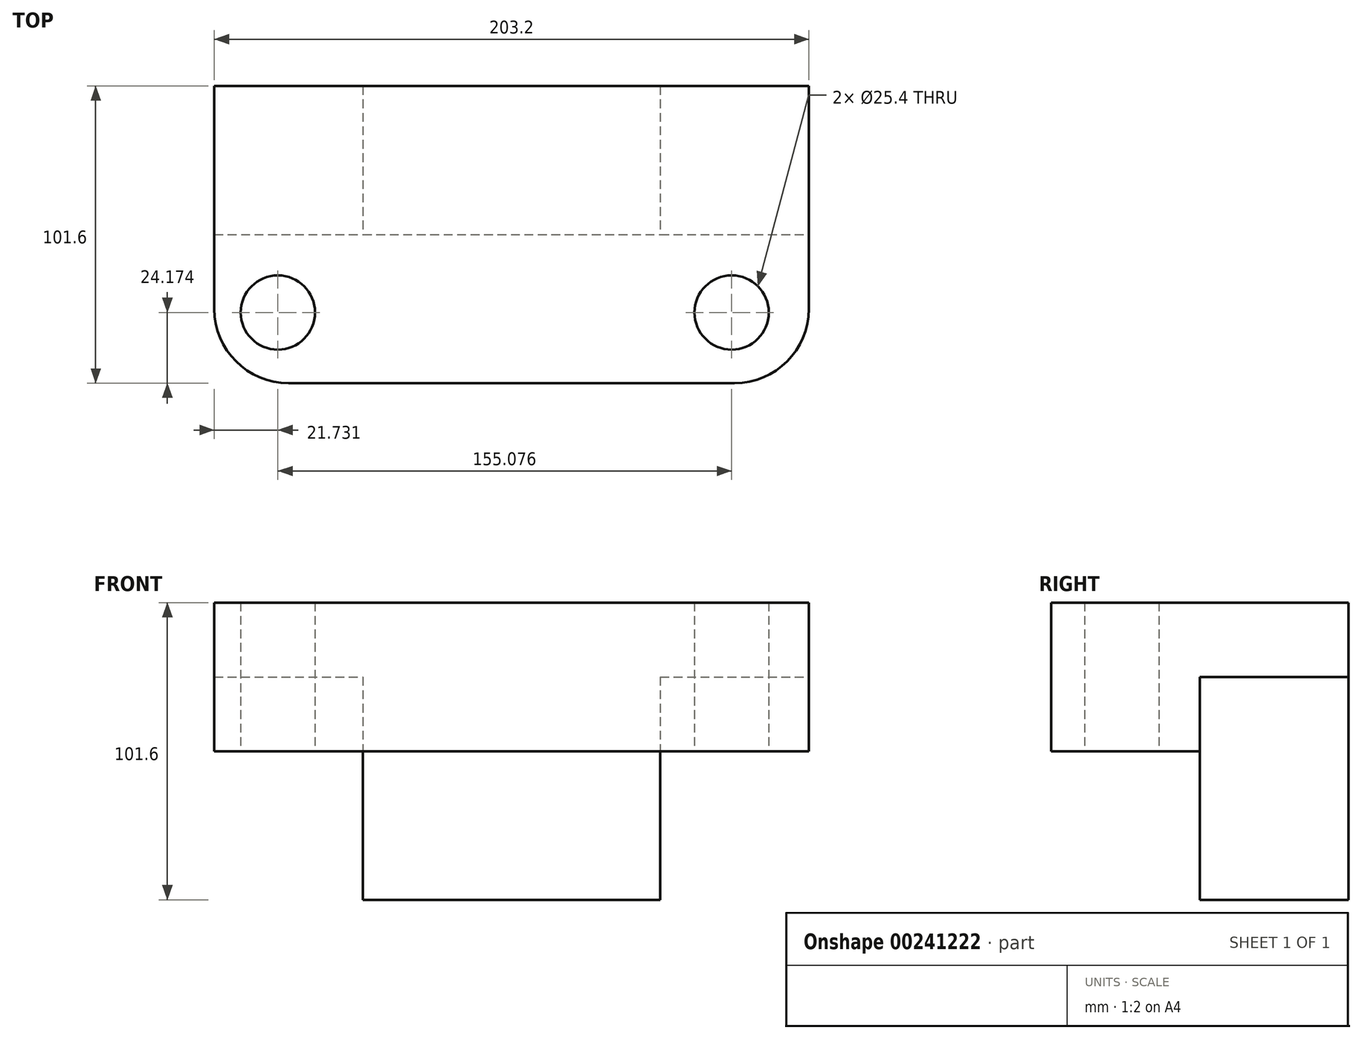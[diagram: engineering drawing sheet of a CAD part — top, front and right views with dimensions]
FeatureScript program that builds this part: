
annotation { "Feature Type Name" : "Feature", "Feature Type Description" : "" }
export const myFeature = defineFeature(function(context is Context, id is Id, definition is map)
    precondition{}
    {
        {
            var Q0;
            Q0=qCreatedBy(makeId("Front.planeOp"),FACE);
            var sketch = newSketch(context, id + "F0", { "sketchPlane" : qUnion([Q0])});
            skLineSegment(sketch, "E0.bottom", {"start": v(-115.86, 69.09) * mm, "end": v(87.34, 69.09) * mm});
            skLineSegment(sketch, "E0.top", {"start": v(-115.86, -32.51) * mm, "end": v(87.34, -32.51) * mm});
            skLineSegment(sketch, "E0.left", {"start": v(-115.86, 69.09) * mm, "end": v(-115.86, -32.51) * mm});
            skLineSegment(sketch, "E0.right", {"start": v(87.34, 69.09) * mm, "end": v(87.34, -32.51) * mm});
            skSolve(sketch);
        }
        {
            var Q0;
            Q0=makeQuery(id+"F0.imprint","IMPRINT",FACE,{"disambiguationData":[TD([[makeQuery(id+"F0.imprint","IMPRINT",EDGE,{"derivedFrom":sQuery(id+"F0.wireOp",EDGE,"E0.bottom")}),-1.0]])]});
            extrude(context, id + "F1", {"entities" : qUnion([Q0]), "depth" : 101.6 * mm});
        }
        {
            var Q0;
            Q0=makeQuery(id+"F1.opExtrude","CAP_FACE",FACE,{"disambiguationData":[OSD([sQuery(id+"F0.wireOp",EDGE,"E0.bottom"),sQuery(id+"F0.wireOp",EDGE,"E0.top"),sQuery(id+"F0.wireOp",EDGE,"E0.left"),sQuery(id+"F0.wireOp",EDGE,"E0.right")])],"isStart":false});
            var sketch = newSketch(context, id + "F2", { "sketchPlane" : qUnion([Q0])});
            skLineSegment(sketch, "E1.bottom", {"start": v(-115.86, -32.51) * mm, "end": v(87.34, -32.51) * mm});
            skLineSegment(sketch, "E1.top", {"start": v(-115.86, 18.29) * mm, "end": v(87.34, 18.29) * mm});
            skLineSegment(sketch, "E1.left", {"start": v(-115.86, -32.51) * mm, "end": v(-115.86, 18.29) * mm});
            skLineSegment(sketch, "E1.right", {"start": v(87.34, -32.51) * mm, "end": v(87.34, 18.29) * mm});
            skSolve(sketch);
        }
        {
            var Q0;
            Q0=makeQuery(id+"F2.imprint","IMPRINT",FACE,{"disambiguationData":[TD([[makeQuery(id+"F2.imprint","IMPRINT",EDGE,{"derivedFrom":sQuery(id+"F2.wireOp",EDGE,"E1.bottom")}),1.0]])]});
            extrude(context, id + "F3", {"entities" : qUnion([Q0]), "operationType" : NewBodyOperationType.REMOVE, "oppositeDirection" : true, "depth" : 50.8 * mm});
        }
        {
            var Q0;
            Q0=makeQuery(id+"F1.opExtrude","SWEPT_FACE",FACE,{"disambiguationData":[OSD([sQuery(id+"F0.wireOp",EDGE,"E0.top")])]});
            var sketch = newSketch(context, id + "F4", { "sketchPlane" : qUnion([Q0])});
            skLineSegment(sketch, "E2.bottom", {"start": v(87.34, 0) * mm, "end": v(36.54, 0) * mm});
            skLineSegment(sketch, "E2.top", {"start": v(87.34, 50.8) * mm, "end": v(36.54, 50.8) * mm});
            skLineSegment(sketch, "E2.left", {"start": v(87.34, 0) * mm, "end": v(87.34, 50.8) * mm});
            skLineSegment(sketch, "E2.right", {"start": v(36.54, 0) * mm, "end": v(36.54, 50.8) * mm});
            skSolve(sketch);
        }
        {
            var Q0;
            Q0=makeQuery(id+"F4.imprint","IMPRINT",FACE,{"disambiguationData":[TD([[makeQuery(id+"F4.imprint","IMPRINT",EDGE,{"derivedFrom":sQuery(id+"F4.wireOp",EDGE,"E2.bottom")}),1.0]])]});
            extrude(context, id + "F5", {"entities" : qUnion([Q0]), "operationType" : NewBodyOperationType.REMOVE, "oppositeDirection" : true, "depth" : 76.2 * mm});
        }
        {
            var Q0;
            Q0=makeQuery(id+"F1.opExtrude","SWEPT_FACE",FACE,{"disambiguationData":[OSD([sQuery(id+"F0.wireOp",EDGE,"E0.top")])]});
            var sketch = newSketch(context, id + "F6", { "sketchPlane" : qUnion([Q0])});
            skLineSegment(sketch, "E3.bottom", {"start": v(-115.86, 0) * mm, "end": v(-65.06, 0) * mm});
            skLineSegment(sketch, "E3.top", {"start": v(-115.86, 50.8) * mm, "end": v(-65.06, 50.8) * mm});
            skLineSegment(sketch, "E3.left", {"start": v(-115.86, 0) * mm, "end": v(-115.86, 50.8) * mm});
            skLineSegment(sketch, "E3.right", {"start": v(-65.06, 0) * mm, "end": v(-65.06, 50.8) * mm});
            skSolve(sketch);
        }
        {
            var Q0;
            Q0=makeQuery(id+"F6.imprint","IMPRINT",FACE,{"disambiguationData":[TD([[makeQuery(id+"F6.imprint","IMPRINT",EDGE,{"derivedFrom":sQuery(id+"F6.wireOp",EDGE,"E3.bottom")}),1.0]])]});
            extrude(context, id + "F7", {"entities" : qUnion([Q0]), "operationType" : NewBodyOperationType.REMOVE, "oppositeDirection" : true, "depth" : 76.2 * mm});
        }
        {
            var Q0;
            Q0=makeQuery(id+"F1.opExtrude","CAP_EDGE",EDGE,{"disambiguationData":[OSD([sQuery(id+"F0.wireOp",EDGE,"E0.right")])],"isStart":false});
            fillet(context, id + "F8", {"entities" : qUnion([Q0]), "radius" : 25.4 * mm, "tangentPropagation" : true, "allowEdgeOverflow" : false});
        }
        {
            var Q0;
            Q0=makeQuery(id+"F1.opExtrude","CAP_EDGE",EDGE,{"disambiguationData":[OSD([sQuery(id+"F0.wireOp",EDGE,"E0.left")])],"isStart":false});
            fillet(context, id + "F9", {"entities" : qUnion([Q0]), "radius" : 25.4 * mm, "tangentPropagation" : true, "allowEdgeOverflow" : false});
        }
        {
            var Q0;
            Q0=makeQuery(id+"F3.boolean.opBoolean","COPY",FACE,{"derivedFrom":makeQuery(id+"F3.opExtrude","SWEPT_FACE",FACE,{"disambiguationData":[OSD([sQuery(id+"F2.wireOp",EDGE,"E1.top")])]})});
            var sketch = newSketch(context, id + "F10", { "sketchPlane" : qUnion([Q0])});
            skCircle(sketch, "E4", {"center": v(-94.13, 77.43) * mm, "radius": 12.7 * mm});
            skSolve(sketch);
        }
        {
            var Q0;
            Q0=makeQuery(id+"F10.imprint","IMPRINT",FACE,{"disambiguationData":[TD([[makeQuery(id+"F10.imprint","IMPRINT",EDGE,{"derivedFrom":sQuery(id+"F10.wireOp",EDGE,"E4")}),-1.0]])]});
            var sketch = newSketch(context, id + "F11", { "sketchPlane" : qUnion([Q0])});
            skCircle(sketch, "E5", {"center": v(60.95, 77.43) * mm, "radius": 12.7 * mm});
            skSolve(sketch);
        }
        {
            var Q0;
            Q0=sQuery(id+"F10.wireOp",VERTEX,"E4.center");
            var Q1;
            Q1=makeQuery(id+"F1.opExtrude","SWEPT_BODY",BODY,{"disambiguationData":[OSD([sQuery(id+"F0.wireOp",EDGE,"E0.bottom"),sQuery(id+"F0.wireOp",EDGE,"E0.top"),sQuery(id+"F0.wireOp",EDGE,"E0.left"),sQuery(id+"F0.wireOp",EDGE,"E0.right")])]});
            hole(context, id + "F12", {"style" : HoleStyle.SIMPLE, "endStyle" : HoleEndStyle.THROUGH, "holeDiameter" : 6.35 * mm, "locations" : qUnion([Q0]), "scope" : qUnion([Q1]), "isTappedThrough" : true});
        }
        {
            var Q0;
            Q0=makeQuery(id+"F11.imprint","IMPRINT",FACE,{"disambiguationData":[TD([[makeQuery(id+"F11.imprint","IMPRINT",EDGE,{"derivedFrom":sQuery(id+"F11.wireOp",EDGE,"E5")}),1.0]])]});
            extrude(context, id + "F13", {"entities" : qUnion([Q0]), "operationType" : NewBodyOperationType.REMOVE, "oppositeDirection" : true, "depth" : 101.6 * mm});
        }
        {
            var Q0;
            Q0=makeQuery(id+"F3.boolean.opBoolean","COPY",FACE,{"derivedFrom":makeQuery(id+"F3.opExtrude","SWEPT_FACE",FACE,{"disambiguationData":[OSD([sQuery(id+"F2.wireOp",EDGE,"E1.top")])]})});
            var sketch = newSketch(context, id + "F14", { "sketchPlane" : qUnion([Q0])});
            skCircle(sketch, "E6", {"center": v(-94.13, 77.43) * mm, "radius": 12.7 * mm});
            skSolve(sketch);
        }
        {
            var Q0;
            Q0=makeQuery(id+"F14.imprint","IMPRINT",FACE,{"disambiguationData":[TD([[makeQuery(id+"F14.imprint","IMPRINT",EDGE,{"derivedFrom":sQuery(id+"F14.wireOp",EDGE,"E6")}),1.0]])]});
            extrude(context, id + "F15", {"entities" : qUnion([Q0]), "operationType" : NewBodyOperationType.REMOVE, "oppositeDirection" : true, "depth" : 101.6 * mm});
        }
    });
